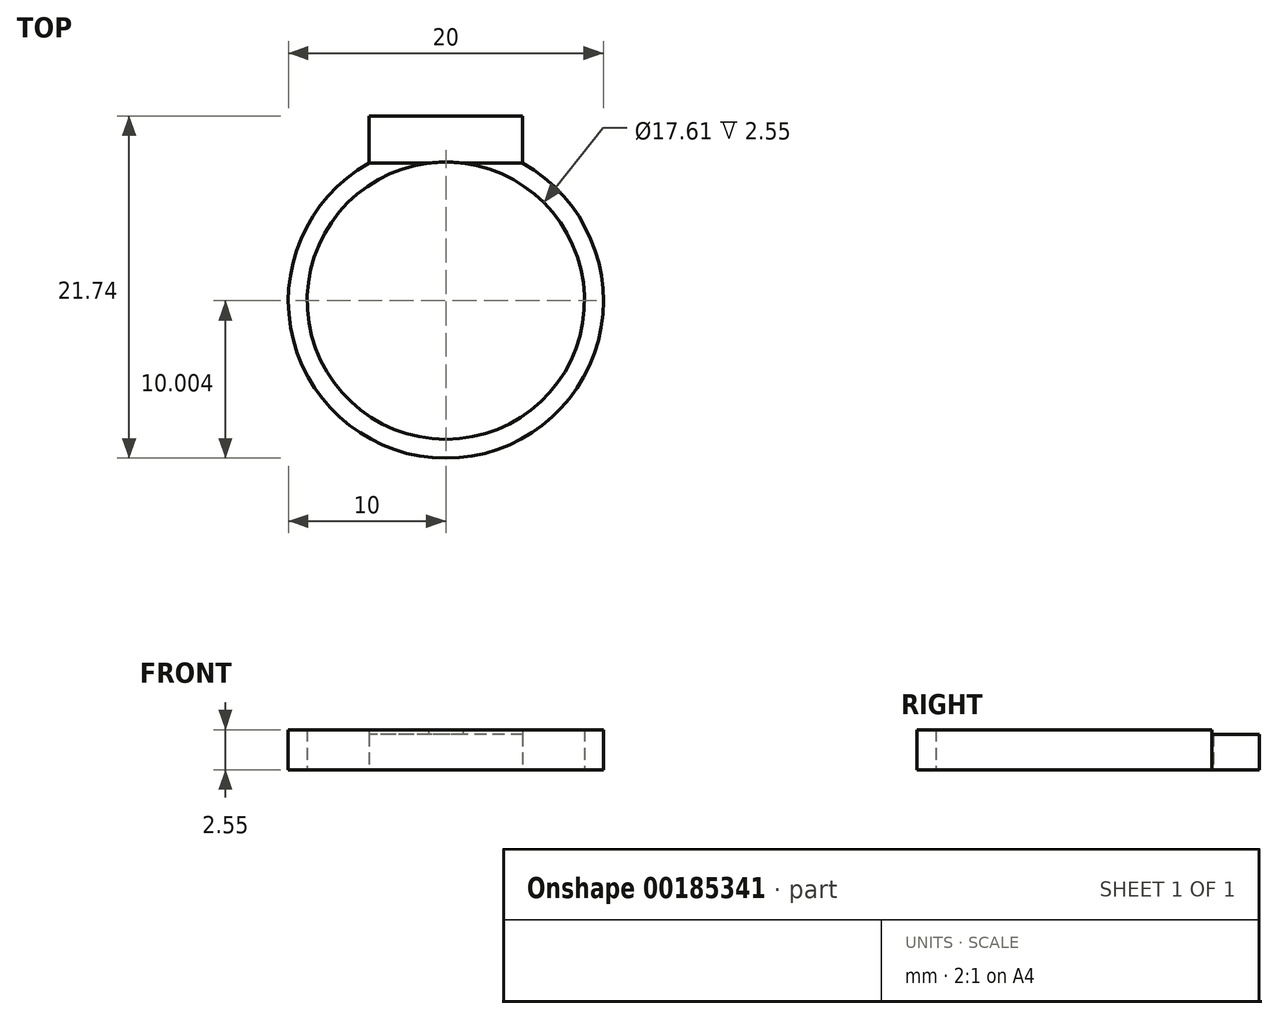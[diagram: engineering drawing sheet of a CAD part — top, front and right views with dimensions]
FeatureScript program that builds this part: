
annotation { "Feature Type Name" : "Feature", "Feature Type Description" : "" }
export const myFeature = defineFeature(function(context is Context, id is Id, definition is map)
    precondition{}
    {
        {
            var Q0;
            Q0=qCreatedBy(makeId("Top.planeOp"),FACE);
            var sketch = newSketch(context, id + "F0", { "sketchPlane" : qUnion([Q0])});
            skLineSegment(sketch, "E0.bottom", {"start": v(4.88, -1.5) * mm, "end": v(-4.88, -1.5) * mm});
            skLineSegment(sketch, "E0.top", {"start": v(4.88, 1.5) * mm, "end": v(-4.88, 1.5) * mm});
            skLineSegment(sketch, "E0.left", {"start": v(4.88, -1.5) * mm, "end": v(4.88, 1.5) * mm});
            skLineSegment(sketch, "E0.right", {"start": v(-4.88, -1.5) * mm, "end": v(-4.88, 1.5) * mm});
            skPoint(sketch, "E0.middle", {"position": v(0, 0) * mm});
            skCircle(sketch, "E1", {"center": v(0, -10.24) * mm, "radius": 10 * mm});
            skPoint(sketch, "E1.third.point", {"position": v(0, -20.24) * mm});
            skCircle(sketch, "E2.0", {"center": v(0, -10.24) * mm, "radius": 8.8 * mm});
            skSolve(sketch);
        }
        {
            var Q0;
            Q0=makeQuery(id+"F0.imprint","IMPRINT",FACE,{"disambiguationData":[TD([[makeQuery(id+"F0.imprint","IMPRINT",EDGE,{"derivedFrom":sQuery(id+"F0.wireOp",EDGE,"E0.top")}),1.0]])]});
            var Q1;
            {var subQ0=sQuery(id+"F0.wireOp",EDGE,"E0.bottom");Q1=makeQuery(id+"F0.imprint","IMPRINT",FACE,{"disambiguationData":[TD([[makeQuery(id+"F0.imprint","IMPRINT",EDGE,{"derivedFrom":subQ0}),-1.0]])]});}
            extrude(context, id + "F1", {"entities" : qUnion([Q0, Q1]), "depth" : 2.25 * mm});
        }
        {
            var Q0;
            {var subQ0=sQuery(id+"F0.wireOp",EDGE,"E0.bottom");Q0=makeQuery(id+"F0.imprint","IMPRINT",FACE,{"disambiguationData":[TD([[makeQuery(id+"F0.imprint","IMPRINT",EDGE,{"derivedFrom":subQ0}),1.0]])]});}
            extrude(context, id + "F2", {"entities" : qUnion([Q0]), "operationType" : NewBodyOperationType.ADD, "depth" : 2.55 * mm});
        }
    });
